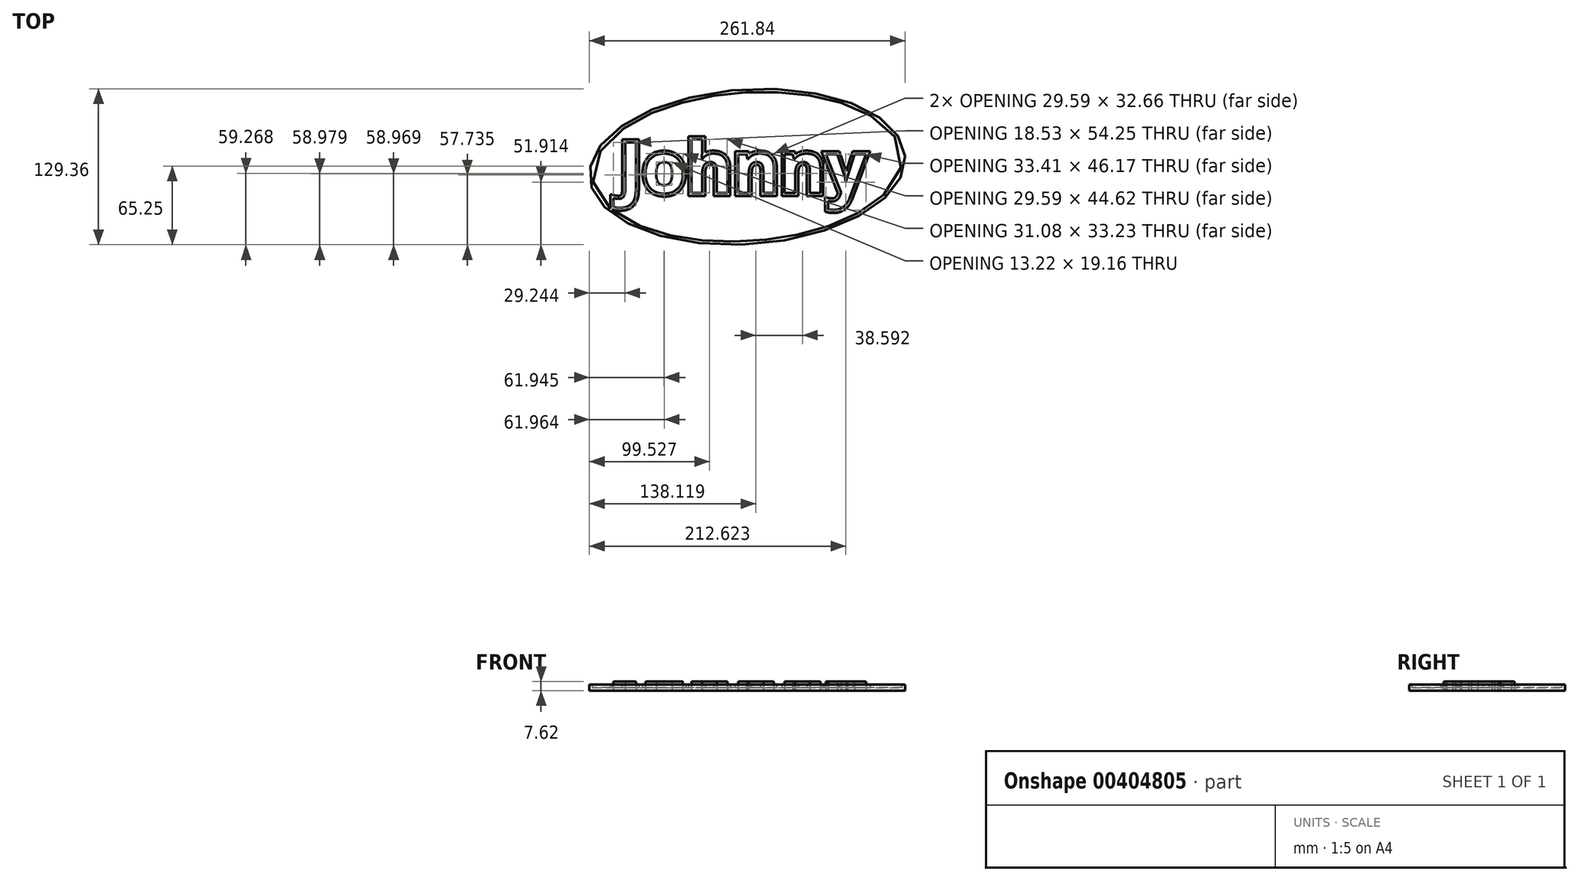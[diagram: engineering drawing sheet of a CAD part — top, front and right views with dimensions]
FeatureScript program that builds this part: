
annotation { "Feature Type Name" : "Feature", "Feature Type Description" : "" }
export const myFeature = defineFeature(function(context is Context, id is Id, definition is map)
    precondition{}
    {
        {
            var Q0;
            Q0=qCreatedBy(makeId("Top.planeOp"),FACE);
            var sketch = newSketch(context, id + "F0", { "sketchPlane" : qUnion([Q0])});
            skText(sketch, "E0", { "text": "Johnny", "fontName": "OpenSans-Bold.ttf"});
            skEllipse(sketch, "E1", {"center": v(-14.81, 0) * mm, "majorRadius": 131.14 * mm, "minorRadius": 64.24 * mm, "majorAxis": v(1, 0.07)});
            const initialGuessF0  = {"E0": [-0.12139, -0.02174, 1, 0, 0.04228]};
            skSetInitialGuess(sketch, initialGuessF0);
            skSolve(sketch);
        }
        {
            var Q0;
            Q0=makeQuery(id+"F0.imprint","IMPRINT",FACE,{"disambiguationData":[TD([[makeQuery(id+"F0.imprint","IMPRINT",EDGE,{"derivedFrom":sQuery(id+"F0.wireOp",EDGE,"E0.sketch_text.stroke-79")}),-1.0]])]});
            var Q1;
            Q1=makeQuery(id+"F0.imprint","IMPRINT",FACE,{"disambiguationData":[TD([[makeQuery(id+"F0.imprint","IMPRINT",EDGE,{"derivedFrom":sQuery(id+"F0.wireOp",EDGE,"E0.sketch_text.stroke-62")}),-1.0]])]});
            var Q2;
            Q2=makeQuery(id+"F0.imprint","IMPRINT",FACE,{"disambiguationData":[TD([[makeQuery(id+"F0.imprint","IMPRINT",EDGE,{"derivedFrom":sQuery(id+"F0.wireOp",EDGE,"E0.sketch_text.stroke-45")}),-1.0]])]});
            var Q3;
            Q3=makeQuery(id+"F0.imprint","IMPRINT",FACE,{"disambiguationData":[TD([[makeQuery(id+"F0.imprint","IMPRINT",EDGE,{"derivedFrom":sQuery(id+"F0.wireOp",EDGE,"E0.sketch_text.stroke-28")}),-1.0]])]});
            var Q4;
            Q4=makeQuery(id+"F0.imprint","IMPRINT",FACE,{"disambiguationData":[TD([[makeQuery(id+"F0.imprint","IMPRINT",EDGE,{"derivedFrom":sQuery(id+"F0.wireOp",EDGE,"E0.sketch_text.stroke-10")}),-1.0]])]});
            var Q5;
            Q5=makeQuery(id+"F0.imprint","IMPRINT",FACE,{"disambiguationData":[TD([[makeQuery(id+"F0.imprint","IMPRINT",EDGE,{"derivedFrom":sQuery(id+"F0.wireOp",EDGE,"E0.sketch_text.stroke-0")}),-1.0]])]});
            extrude(context, id + "F1", {"entities" : qUnion([Q0, Q1, Q2, Q3, Q4, Q5]), "depth" : 7.62 * mm});
        }
        {
            var Q0;
            Q0=makeQuery(id+"F0.imprint","IMPRINT",FACE,{"disambiguationData":[TD([[makeQuery(id+"F0.imprint","IMPRINT",EDGE,{"derivedFrom":sQuery(id+"F0.wireOp",EDGE,"E0.sketch_text.stroke-0")}),1.0]])]});
            extrude(context, id + "F2", {"entities" : qUnion([Q0]), "depth" : 5 * mm});
        }
        {
            var Q0;
            Q0=makeQuery(id+"F2.opExtrude","CAP_FACE",FACE,{"disambiguationData":[OSD([sQuery(id+"F0.wireOp",EDGE,"E0.sketch_text.stroke-0"),sQuery(id+"F0.wireOp",EDGE,"E0.sketch_text.stroke-1"),sQuery(id+"F0.wireOp",EDGE,"E0.sketch_text.stroke-2"),sQuery(id+"F0.wireOp",EDGE,"E0.sketch_text.stroke-3"),sQuery(id+"F0.wireOp",EDGE,"E0.sketch_text.stroke-4"),sQuery(id+"F0.wireOp",EDGE,"E0.sketch_text.stroke-5"),sQuery(id+"F0.wireOp",EDGE,"E0.sketch_text.stroke-6"),sQuery(id+"F0.wireOp",EDGE,"E0.sketch_text.stroke-7"),sQuery(id+"F0.wireOp",EDGE,"E0.sketch_text.stroke-8"),sQuery(id+"F0.wireOp",EDGE,"E0.sketch_text.stroke-9"),sQuery(id+"F0.wireOp",EDGE,"E0.sketch_text.stroke-18"),sQuery(id+"F0.wireOp",EDGE,"E0.sketch_text.stroke-19"),sQuery(id+"F0.wireOp",EDGE,"E0.sketch_text.stroke-20"),sQuery(id+"F0.wireOp",EDGE,"E0.sketch_text.stroke-21"),sQuery(id+"F0.wireOp",EDGE,"E0.sketch_text.stroke-22"),sQuery(id+"F0.wireOp",EDGE,"E0.sketch_text.stroke-23"),sQuery(id+"F0.wireOp",EDGE,"E0.sketch_text.stroke-24"),sQuery(id+"F0.wireOp",EDGE,"E0.sketch_text.stroke-25"),sQuery(id+"F0.wireOp",EDGE,"E0.sketch_text.stroke-26"),sQuery(id+"F0.wireOp",EDGE,"E0.sketch_text.stroke-27"),sQuery(id+"F0.wireOp",EDGE,"E0.sketch_text.stroke-28"),sQuery(id+"F0.wireOp",EDGE,"E0.sketch_text.stroke-29"),sQuery(id+"F0.wireOp",EDGE,"E0.sketch_text.stroke-30"),sQuery(id+"F0.wireOp",EDGE,"E0.sketch_text.stroke-31"),sQuery(id+"F0.wireOp",EDGE,"E0.sketch_text.stroke-32"),sQuery(id+"F0.wireOp",EDGE,"E0.sketch_text.stroke-33"),sQuery(id+"F0.wireOp",EDGE,"E0.sketch_text.stroke-34"),sQuery(id+"F0.wireOp",EDGE,"E0.sketch_text.stroke-35"),sQuery(id+"F0.wireOp",EDGE,"E0.sketch_text.stroke-36"),sQuery(id+"F0.wireOp",EDGE,"E0.sketch_text.stroke-37"),sQuery(id+"F0.wireOp",EDGE,"E0.sketch_text.stroke-38"),sQuery(id+"F0.wireOp",EDGE,"E0.sketch_text.stroke-39"),sQuery(id+"F0.wireOp",EDGE,"E0.sketch_text.stroke-40"),sQuery(id+"F0.wireOp",EDGE,"E0.sketch_text.stroke-41"),sQuery(id+"F0.wireOp",EDGE,"E0.sketch_text.stroke-42"),sQuery(id+"F0.wireOp",EDGE,"E0.sketch_text.stroke-43"),sQuery(id+"F0.wireOp",EDGE,"E0.sketch_text.stroke-44"),sQuery(id+"F0.wireOp",EDGE,"E0.sketch_text.stroke-45"),sQuery(id+"F0.wireOp",EDGE,"E0.sketch_text.stroke-46"),sQuery(id+"F0.wireOp",EDGE,"E0.sketch_text.stroke-47"),sQuery(id+"F0.wireOp",EDGE,"E0.sketch_text.stroke-48"),sQuery(id+"F0.wireOp",EDGE,"E0.sketch_text.stroke-49"),sQuery(id+"F0.wireOp",EDGE,"E0.sketch_text.stroke-50"),sQuery(id+"F0.wireOp",EDGE,"E0.sketch_text.stroke-51"),sQuery(id+"F0.wireOp",EDGE,"E0.sketch_text.stroke-52"),sQuery(id+"F0.wireOp",EDGE,"E0.sketch_text.stroke-53"),sQuery(id+"F0.wireOp",EDGE,"E0.sketch_text.stroke-54"),sQuery(id+"F0.wireOp",EDGE,"E0.sketch_text.stroke-55"),sQuery(id+"F0.wireOp",EDGE,"E0.sketch_text.stroke-56"),sQuery(id+"F0.wireOp",EDGE,"E0.sketch_text.stroke-57"),sQuery(id+"F0.wireOp",EDGE,"E0.sketch_text.stroke-58"),sQuery(id+"F0.wireOp",EDGE,"E0.sketch_text.stroke-59"),sQuery(id+"F0.wireOp",EDGE,"E0.sketch_text.stroke-60"),sQuery(id+"F0.wireOp",EDGE,"E0.sketch_text.stroke-61"),sQuery(id+"F0.wireOp",EDGE,"E0.sketch_text.stroke-62"),sQuery(id+"F0.wireOp",EDGE,"E0.sketch_text.stroke-63"),sQuery(id+"F0.wireOp",EDGE,"E0.sketch_text.stroke-64"),sQuery(id+"F0.wireOp",EDGE,"E0.sketch_text.stroke-65"),sQuery(id+"F0.wireOp",EDGE,"E0.sketch_text.stroke-66"),sQuery(id+"F0.wireOp",EDGE,"E0.sketch_text.stroke-67"),sQuery(id+"F0.wireOp",EDGE,"E0.sketch_text.stroke-68"),sQuery(id+"F0.wireOp",EDGE,"E0.sketch_text.stroke-69"),sQuery(id+"F0.wireOp",EDGE,"E0.sketch_text.stroke-70"),sQuery(id+"F0.wireOp",EDGE,"E0.sketch_text.stroke-71"),sQuery(id+"F0.wireOp",EDGE,"E0.sketch_text.stroke-72"),sQuery(id+"F0.wireOp",EDGE,"E0.sketch_text.stroke-73"),sQuery(id+"F0.wireOp",EDGE,"E0.sketch_text.stroke-74"),sQuery(id+"F0.wireOp",EDGE,"E0.sketch_text.stroke-75"),sQuery(id+"F0.wireOp",EDGE,"E0.sketch_text.stroke-76"),sQuery(id+"F0.wireOp",EDGE,"E0.sketch_text.stroke-77"),sQuery(id+"F0.wireOp",EDGE,"E0.sketch_text.stroke-78"),sQuery(id+"F0.wireOp",EDGE,"E0.sketch_text.stroke-79"),sQuery(id+"F0.wireOp",EDGE,"E0.sketch_text.stroke-80"),sQuery(id+"F0.wireOp",EDGE,"E0.sketch_text.stroke-81"),sQuery(id+"F0.wireOp",EDGE,"E0.sketch_text.stroke-82"),sQuery(id+"F0.wireOp",EDGE,"E0.sketch_text.stroke-83"),sQuery(id+"F0.wireOp",EDGE,"E0.sketch_text.stroke-84"),sQuery(id+"F0.wireOp",EDGE,"E0.sketch_text.stroke-85"),sQuery(id+"F0.wireOp",EDGE,"E0.sketch_text.stroke-86"),sQuery(id+"F0.wireOp",EDGE,"E0.sketch_text.stroke-87"),sQuery(id+"F0.wireOp",EDGE,"E0.sketch_text.stroke-88"),sQuery(id+"F0.wireOp",EDGE,"E0.sketch_text.stroke-89"),sQuery(id+"F0.wireOp",EDGE,"E0.sketch_text.stroke-90"),sQuery(id+"F0.wireOp",EDGE,"E0.sketch_text.stroke-91"),sQuery(id+"F0.wireOp",EDGE,"E0.sketch_text.stroke-92"),sQuery(id+"F0.wireOp",EDGE,"E0.sketch_text.stroke-93"),sQuery(id+"F0.wireOp",EDGE,"E0.sketch_text.stroke-94"),sQuery(id+"F0.wireOp",EDGE,"E0.sketch_text.stroke-95"),sQuery(id+"F0.wireOp",EDGE,"E1")])],"isStart":false});
            shell(context, id + "F3", {"entities" : qUnion([Q0]), "thickness" : 2.5 * mm});
        }
    });
